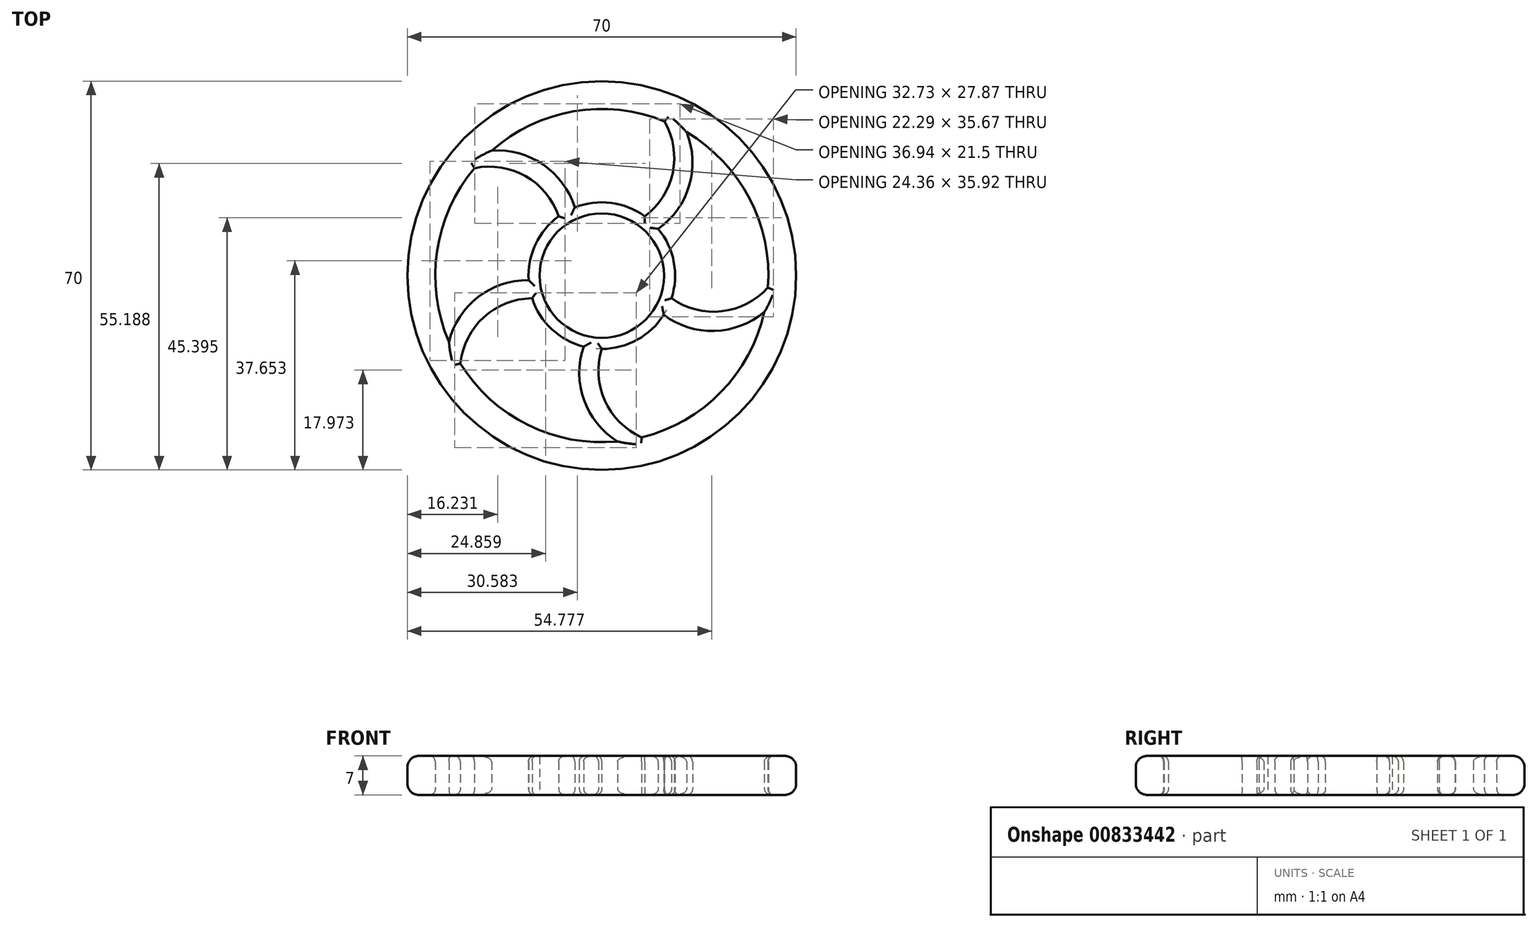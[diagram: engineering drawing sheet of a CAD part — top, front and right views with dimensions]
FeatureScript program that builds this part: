
annotation { "Feature Type Name" : "Feature", "Feature Type Description" : "" }
export const myFeature = defineFeature(function(context is Context, id is Id, definition is map)
    precondition{}
    {
        {
            var Q0;
            Q0=qCreatedBy(makeId("Top.planeOp"),FACE);
            var sketch = newSketch(context, id + "F0", { "sketchPlane" : qUnion([Q0])});
            skCircle(sketch, "E0", {"center": v(0, 0) * mm, "radius": 11.2 * mm});
            skArc(sketch, "E1", {"start": v(-12.55, -4.08) * mm, "mid": v(-9.03, -9.63) * mm, "end": v(-3.27, -12.79) * mm});
            skCircle(sketch, "E2", {"center": v(0, 0) * mm, "radius": 35 * mm});
            skArc(sketch, "E3", {"start": v(-22.93, 19.34) * mm, "mid": v(-29.68, 4.37) * mm, "end": v(-27.53, -11.92) * mm});
            skArc(sketch, "E4", {"start": v(0, -13.2) * mm, "mid": v(0.57, -22.53) * mm, "end": v(7.18, -29.13) * mm});
            skArc(sketch, "E5", {"start": v(-3.27, -12.79) * mm, "mid": v(-3.2, -22.4) * mm, "end": v(2.83, -29.87) * mm});
            skArc(sketch, "E6.1.0", {"start": v(11.15, -7.06) * mm, "mid": v(20.3, -9.96) * mm, "end": v(29.28, -6.54) * mm});
            skArc(sketch, "E6.1.1", {"start": v(12.55, -4.08) * mm, "mid": v(21.6, -6.42) * mm, "end": v(29.92, -2.17) * mm});
            skArc(sketch, "E6.2.0", {"start": v(10.16, 8.42) * mm, "mid": v(15.75, 16.23) * mm, "end": v(15.27, 25.83) * mm});
            skArc(sketch, "E6.2.1", {"start": v(7.76, 10.68) * mm, "mid": v(12.78, 18.56) * mm, "end": v(11.3, 27.79) * mm});
            skArc(sketch, "E6.3.0", {"start": v(-4.87, 12.27) * mm, "mid": v(-10.57, 20) * mm, "end": v(-19.84, 22.5) * mm});
            skArc(sketch, "E6.3.1", {"start": v(-7.76, 10.68) * mm, "mid": v(-13.7, 17.9) * mm, "end": v(-22.93, 19.34) * mm});
            skArc(sketch, "E6.4.0", {"start": v(-13.17, -0.84) * mm, "mid": v(-22.28, -3.88) * mm, "end": v(-27.53, -11.92) * mm});
            skArc(sketch, "E6.4.1", {"start": v(-12.55, -4.08) * mm, "mid": v(-21.25, -7.5) * mm, "end": v(-25.48, -15.83) * mm});
            skArc(sketch, "E7.trimOffspring", {"start": v(11.3, 27.79) * mm, "mid": v(-5.02, 29.58) * mm, "end": v(-19.84, 22.5) * mm});
            skArc(sketch, "E8.trimOffspring", {"start": v(29.92, -2.17) * mm, "mid": v(26.58, 13.91) * mm, "end": v(15.27, 25.83) * mm});
            skArc(sketch, "E9.trimOffspring", {"start": v(7.18, -29.13) * mm, "mid": v(21.45, -20.98) * mm, "end": v(29.28, -6.54) * mm});
            skArc(sketch, "E10.trimOffspring", {"start": v(-25.48, -15.83) * mm, "mid": v(-13.32, -26.88) * mm, "end": v(2.83, -29.87) * mm});
            skArc(sketch, "E11.trimOffspring", {"start": v(-7.76, 10.68) * mm, "mid": v(-11.95, 5.62) * mm, "end": v(-13.17, -0.84) * mm});
            skArc(sketch, "E12.trimOffspring", {"start": v(7.76, 10.68) * mm, "mid": v(1.65, 13.1) * mm, "end": v(-4.87, 12.27) * mm});
            skArc(sketch, "E13.trimOffspring", {"start": v(12.55, -4.08) * mm, "mid": v(12.97, 2.48) * mm, "end": v(10.16, 8.42) * mm});
            skArc(sketch, "E14.trimOffspring", {"start": v(0, -13.2) * mm, "mid": v(6.36, -11.56) * mm, "end": v(11.15, -7.06) * mm});
            skSolve(sketch);
        }
        {
            var Q0;
            Q0=makeQuery(id+"F0.imprint","IMPRINT",FACE,{"disambiguationData":[TD([[makeQuery(id+"F0.imprint","IMPRINT",EDGE,{"derivedFrom":sQuery(id+"F0.wireOp",EDGE,"E2")}),1.0]])]});
            var Q1;
            Q1=makeQuery(id+"F0.imprint","IMPRINT",FACE,{"disambiguationData":[TD([[makeQuery(id+"F0.imprint","IMPRINT",EDGE,{"derivedFrom":sQuery(id+"F0.wireOp",EDGE,"E0")}),-1.0]])]});
            extrude(context, id + "F1", {"entities" : qUnion([Q0, Q1]), "depth" : 7 * mm, "offsetDistance" : 25 * mm});
        }
        {
            var Q0;
            Q0=makeQuery(id+"F1.opExtrude","CAP_EDGE",EDGE,{"disambiguationData":[OSD([sQuery(id+"F0.wireOp",EDGE,"E6.3.1")])],"isStart":false});
            var Q1;
            Q1=makeQuery(id+"F1.opExtrude","CAP_EDGE",EDGE,{"disambiguationData":[OSD([sQuery(id+"F0.wireOp",EDGE,"E6.3.0")])],"isStart":false});
            var Q2;
            Q2=makeQuery(id+"F1.opExtrude","CAP_EDGE",EDGE,{"disambiguationData":[OSD([sQuery(id+"F0.wireOp",EDGE,"E7.trimOffspring")])],"isStart":false});
            var Q3;
            Q3=makeQuery(id+"F1.opExtrude","CAP_EDGE",EDGE,{"disambiguationData":[OSD([sQuery(id+"F0.wireOp",EDGE,"E6.2.1")])],"isStart":false});
            var Q4;
            Q4=makeQuery(id+"F1.opExtrude","CAP_EDGE",EDGE,{"disambiguationData":[OSD([sQuery(id+"F0.wireOp",EDGE,"E6.2.0")])],"isStart":false});
            var Q5;
            Q5=makeQuery(id+"F1.opExtrude","CAP_EDGE",EDGE,{"disambiguationData":[OSD([sQuery(id+"F0.wireOp",EDGE,"E8.trimOffspring")])],"isStart":false});
            var Q6;
            Q6=makeQuery(id+"F1.opExtrude","CAP_EDGE",EDGE,{"disambiguationData":[OSD([sQuery(id+"F0.wireOp",EDGE,"E6.1.1")])],"isStart":false});
            var Q7;
            Q7=makeQuery(id+"F1.opExtrude","CAP_EDGE",EDGE,{"disambiguationData":[OSD([sQuery(id+"F0.wireOp",EDGE,"E6.1.0")])],"isStart":false});
            var Q8;
            Q8=makeQuery(id+"F1.opExtrude","CAP_EDGE",EDGE,{"disambiguationData":[OSD([sQuery(id+"F0.wireOp",EDGE,"E9.trimOffspring")])],"isStart":false});
            var Q9;
            Q9=makeQuery(id+"F1.opExtrude","CAP_EDGE",EDGE,{"disambiguationData":[OSD([sQuery(id+"F0.wireOp",EDGE,"E4")])],"isStart":false});
            var Q10;
            Q10=makeQuery(id+"F1.opExtrude","CAP_EDGE",EDGE,{"disambiguationData":[OSD([sQuery(id+"F0.wireOp",EDGE,"E5")])],"isStart":false});
            var Q11;
            Q11=makeQuery(id+"F1.opExtrude","CAP_EDGE",EDGE,{"disambiguationData":[OSD([sQuery(id+"F0.wireOp",EDGE,"E10.trimOffspring")])],"isStart":false});
            var Q12;
            Q12=makeQuery(id+"F1.opExtrude","CAP_EDGE",EDGE,{"disambiguationData":[OSD([sQuery(id+"F0.wireOp",EDGE,"E6.4.1")])],"isStart":false});
            var Q13;
            Q13=makeQuery(id+"F1.opExtrude","CAP_EDGE",EDGE,{"disambiguationData":[OSD([sQuery(id+"F0.wireOp",EDGE,"E6.4.0")])],"isStart":false});
            var Q14;
            Q14=makeQuery(id+"F1.opExtrude","CAP_EDGE",EDGE,{"disambiguationData":[OSD([sQuery(id+"F0.wireOp",EDGE,"E3")])],"isStart":false});
            var Q15;
            Q15=makeQuery(id+"F1.opExtrude","CAP_EDGE",EDGE,{"disambiguationData":[OSD([sQuery(id+"F0.wireOp",EDGE,"E11.trimOffspring")])],"isStart":false});
            var Q16;
            Q16=makeQuery(id+"F1.opExtrude","CAP_EDGE",EDGE,{"disambiguationData":[OSD([sQuery(id+"F0.wireOp",EDGE,"E12.trimOffspring")])],"isStart":false});
            var Q17;
            Q17=makeQuery(id+"F1.opExtrude","CAP_EDGE",EDGE,{"disambiguationData":[OSD([sQuery(id+"F0.wireOp",EDGE,"E13.trimOffspring")])],"isStart":false});
            var Q18;
            Q18=makeQuery(id+"F1.opExtrude","CAP_EDGE",EDGE,{"disambiguationData":[OSD([sQuery(id+"F0.wireOp",EDGE,"E14.trimOffspring")])],"isStart":false});
            var Q19;
            Q19=makeQuery(id+"F1.opExtrude","CAP_EDGE",EDGE,{"disambiguationData":[OSD([sQuery(id+"F0.wireOp",EDGE,"E1")])],"isStart":false});
            var Q20;
            Q20=makeQuery(id+"F1.opExtrude","CAP_EDGE",EDGE,{"disambiguationData":[OSD([sQuery(id+"F0.wireOp",EDGE,"E10.trimOffspring")])],"isStart":true});
            var Q21;
            Q21=makeQuery(id+"F1.opExtrude","CAP_EDGE",EDGE,{"disambiguationData":[OSD([sQuery(id+"F0.wireOp",EDGE,"E5")])],"isStart":true});
            var Q22;
            Q22=makeQuery(id+"F1.opExtrude","CAP_EDGE",EDGE,{"disambiguationData":[OSD([sQuery(id+"F0.wireOp",EDGE,"E4")])],"isStart":true});
            var Q23;
            Q23=makeQuery(id+"F1.opExtrude","CAP_EDGE",EDGE,{"disambiguationData":[OSD([sQuery(id+"F0.wireOp",EDGE,"E9.trimOffspring")])],"isStart":true});
            var Q24;
            Q24=makeQuery(id+"F1.opExtrude","CAP_EDGE",EDGE,{"disambiguationData":[OSD([sQuery(id+"F0.wireOp",EDGE,"E6.1.0")])],"isStart":true});
            var Q25;
            Q25=makeQuery(id+"F1.opExtrude","CAP_EDGE",EDGE,{"disambiguationData":[OSD([sQuery(id+"F0.wireOp",EDGE,"E6.1.1")])],"isStart":true});
            var Q26;
            Q26=makeQuery(id+"F1.opExtrude","CAP_EDGE",EDGE,{"disambiguationData":[OSD([sQuery(id+"F0.wireOp",EDGE,"E13.trimOffspring")])],"isStart":true});
            var Q27;
            Q27=makeQuery(id+"F1.opExtrude","CAP_EDGE",EDGE,{"disambiguationData":[OSD([sQuery(id+"F0.wireOp",EDGE,"E8.trimOffspring")])],"isStart":true});
            var Q28;
            Q28=makeQuery(id+"F1.opExtrude","CAP_EDGE",EDGE,{"disambiguationData":[OSD([sQuery(id+"F0.wireOp",EDGE,"E6.2.0")])],"isStart":true});
            var Q29;
            Q29=makeQuery(id+"F1.opExtrude","CAP_EDGE",EDGE,{"disambiguationData":[OSD([sQuery(id+"F0.wireOp",EDGE,"E6.2.1")])],"isStart":true});
            var Q30;
            Q30=makeQuery(id+"F1.opExtrude","CAP_EDGE",EDGE,{"disambiguationData":[OSD([sQuery(id+"F0.wireOp",EDGE,"E7.trimOffspring")])],"isStart":true});
            var Q31;
            Q31=makeQuery(id+"F1.opExtrude","CAP_EDGE",EDGE,{"disambiguationData":[OSD([sQuery(id+"F0.wireOp",EDGE,"E6.3.0")])],"isStart":true});
            var Q32;
            Q32=makeQuery(id+"F1.opExtrude","CAP_EDGE",EDGE,{"disambiguationData":[OSD([sQuery(id+"F0.wireOp",EDGE,"E6.3.1")])],"isStart":true});
            var Q33;
            Q33=makeQuery(id+"F1.opExtrude","CAP_EDGE",EDGE,{"disambiguationData":[OSD([sQuery(id+"F0.wireOp",EDGE,"E12.trimOffspring")])],"isStart":true});
            var Q34;
            Q34=makeQuery(id+"F1.opExtrude","CAP_EDGE",EDGE,{"disambiguationData":[OSD([sQuery(id+"F0.wireOp",EDGE,"E11.trimOffspring")])],"isStart":true});
            var Q35;
            Q35=makeQuery(id+"F1.opExtrude","CAP_EDGE",EDGE,{"disambiguationData":[OSD([sQuery(id+"F0.wireOp",EDGE,"E6.4.0")])],"isStart":true});
            var Q36;
            Q36=makeQuery(id+"F1.opExtrude","CAP_EDGE",EDGE,{"disambiguationData":[OSD([sQuery(id+"F0.wireOp",EDGE,"E6.4.1")])],"isStart":true});
            var Q37;
            Q37=makeQuery(id+"F1.opExtrude","CAP_EDGE",EDGE,{"disambiguationData":[OSD([sQuery(id+"F0.wireOp",EDGE,"E3")])],"isStart":true});
            var Q38;
            Q38=makeQuery(id+"F1.opExtrude","CAP_EDGE",EDGE,{"disambiguationData":[OSD([sQuery(id+"F0.wireOp",EDGE,"E1")])],"isStart":true});
            fillet(context, id + "F2", {"entities" : qUnion([Q0, Q1, Q2, Q3, Q4, Q5, Q6, Q7, Q8, Q9, Q10, Q11, Q12, Q13, Q14, Q15, Q16, Q17, Q18, Q19, Q20, Q21, Q22, Q23, Q24, Q25, Q26, Q27, Q28, Q29, Q30, Q31, Q32, Q33, Q34, Q35, Q36, Q37, Q38]), "radius" : 1 * mm, "tangentPropagation" : true, "allowEdgeOverflow" : false});
        }
        {
            var Q0;
            Q0=makeQuery(id+"F1.opExtrude","CAP_EDGE",EDGE,{"disambiguationData":[OSD([sQuery(id+"F0.wireOp",EDGE,"E2")])],"isStart":false});
            var Q1;
            Q1=makeQuery(id+"F1.opExtrude","CAP_EDGE",EDGE,{"disambiguationData":[OSD([sQuery(id+"F0.wireOp",EDGE,"E2")])],"isStart":true});
            fillet(context, id + "F3", {"entities" : qUnion([Q0, Q1]), "radius" : 2 * mm, "tangentPropagation" : true, "allowEdgeOverflow" : false});
        }
    });
